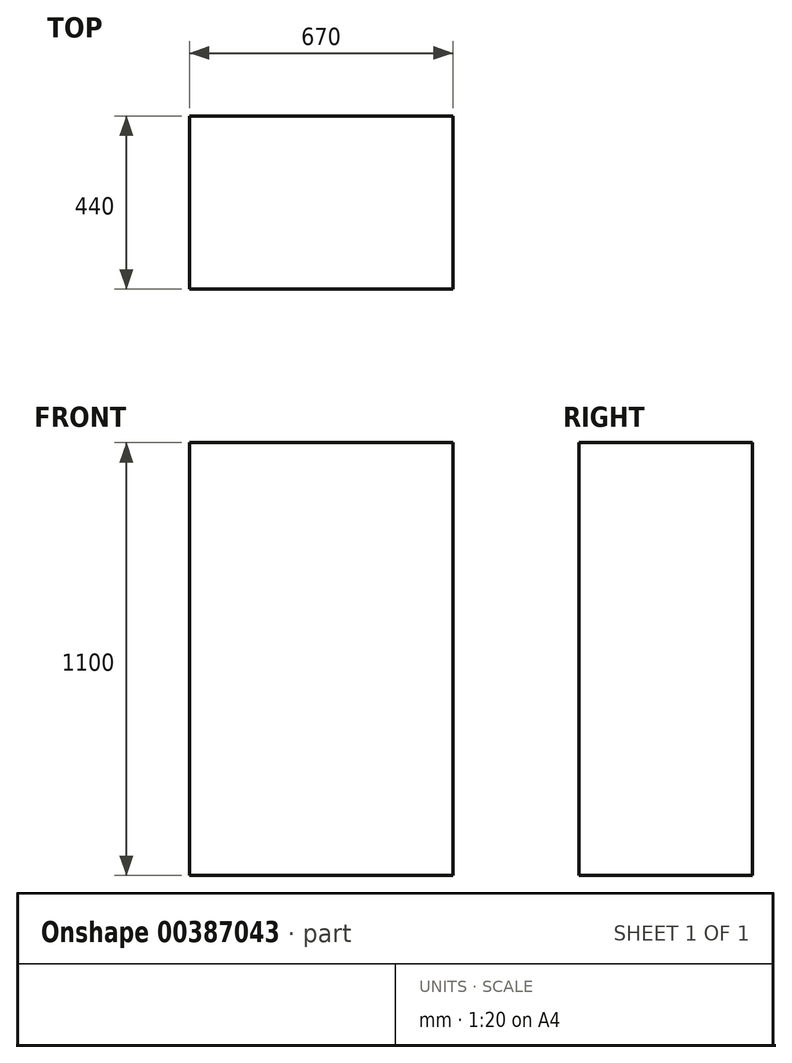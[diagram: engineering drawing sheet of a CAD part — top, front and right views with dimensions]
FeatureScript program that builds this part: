
annotation { "Feature Type Name" : "Feature", "Feature Type Description" : "" }
export const myFeature = defineFeature(function(context is Context, id is Id, definition is map)
    precondition{}
    {
        {
            var Q0;
            Q0=qCreatedBy(makeId("Top.planeOp"),FACE);
            var sketch = newSketch(context, id + "F0", { "sketchPlane" : qUnion([Q0])});
            skLineSegment(sketch, "E0.bottom", {"start": v(0, 0) * mm, "end": v(670, 0) * mm});
            skLineSegment(sketch, "E0.top", {"start": v(0, 440) * mm, "end": v(670, 440) * mm});
            skLineSegment(sketch, "E0.left", {"start": v(0, 0) * mm, "end": v(0, 440) * mm});
            skLineSegment(sketch, "E0.right", {"start": v(670, 0) * mm, "end": v(670, 440) * mm});
            skSolve(sketch);
        }
        {
            var Q0;
            Q0 = qSketchRegion(id + "F0", true);
            extrude(context, id + "F1", {"entities" : qUnion([Q0]), "depth" : 1100 * mm});
        }
    });
